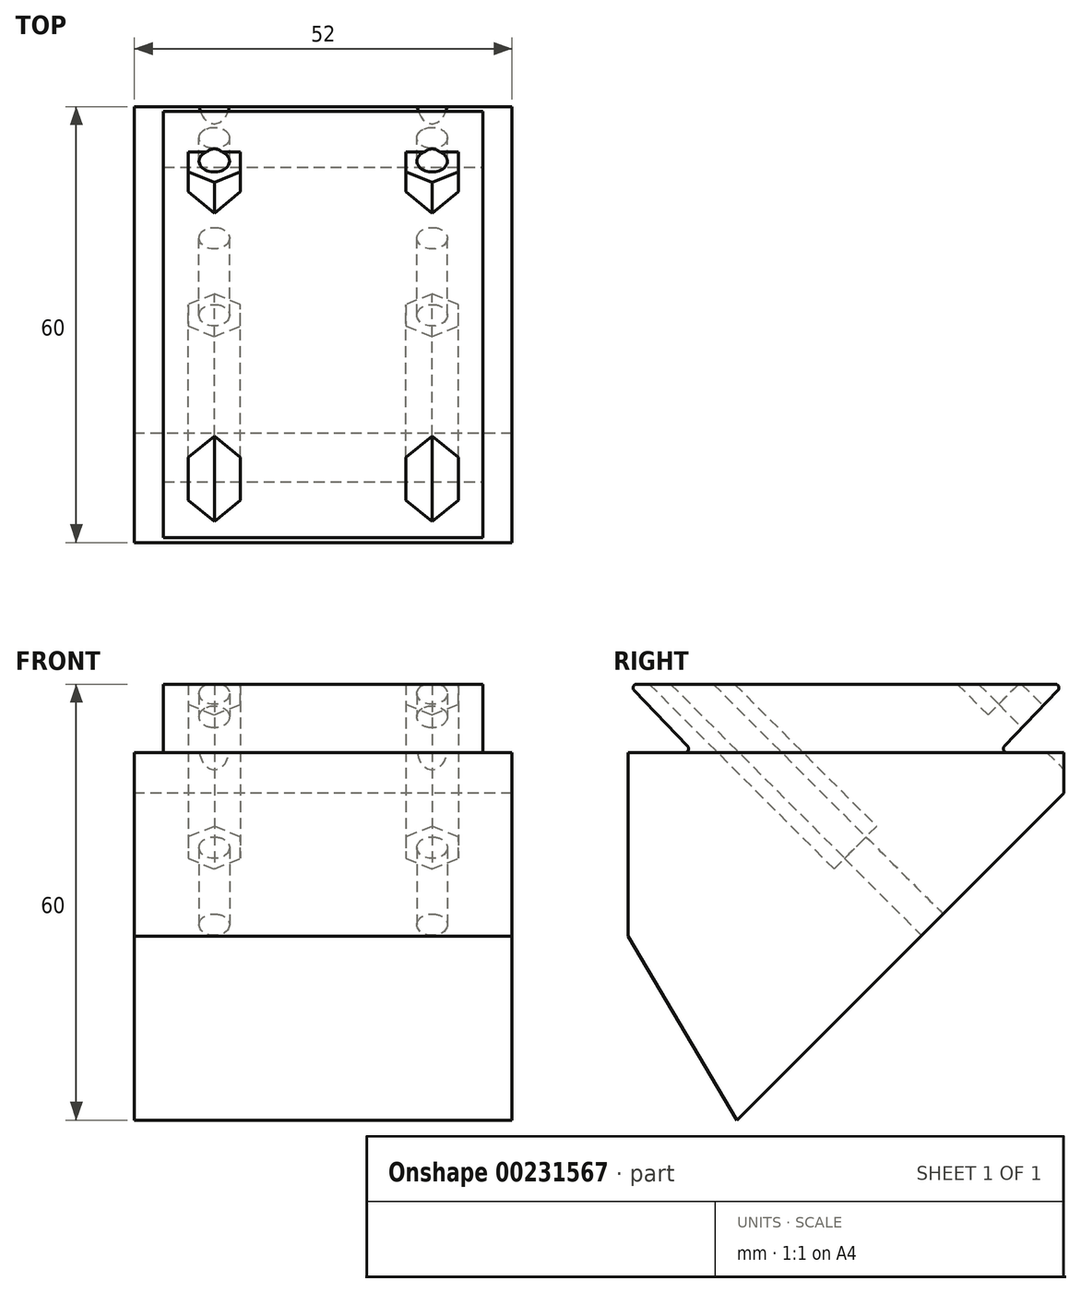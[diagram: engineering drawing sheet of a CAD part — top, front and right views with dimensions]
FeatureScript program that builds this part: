
annotation { "Feature Type Name" : "Feature", "Feature Type Description" : "" }
export const myFeature = defineFeature(function(context is Context, id is Id, definition is map)
    precondition{}
    {
        {
            var Q0;
            Q0=qCreatedBy(makeId("Top.planeOp"),FACE);
            var sketch = newSketch(context, id + "F0", { "sketchPlane" : qUnion([Q0])});
            skLineSegment(sketch, "E0.bottom", {"start": v(26, -30) * mm, "end": v(-26, -30) * mm});
            skLineSegment(sketch, "E0.top", {"start": v(26, 30) * mm, "end": v(-26, 30) * mm});
            skLineSegment(sketch, "E0.left", {"start": v(26, -30) * mm, "end": v(26, 30) * mm});
            skLineSegment(sketch, "E0.right", {"start": v(-26, -30) * mm, "end": v(-26, 30) * mm});
            skPoint(sketch, "E0.middle", {"position": v(0, 0) * mm});
            skSolve(sketch);
        }
        {
            var Q0;
            Q0=makeQuery(id+"F0.imprint","IMPRINT",FACE,{"disambiguationData":[TD([[makeQuery(id+"F0.imprint","IMPRINT",EDGE,{"derivedFrom":sQuery(id+"F0.wireOp",EDGE,"E0.bottom")}),-1.0]])]});
            extrude(context, id + "F1", {"entities" : qUnion([Q0]), "depth" : 15 * mm});
        }
        {
            var Q0;
            Q0=makeQuery(id+"F1.opExtrude","SWEPT_FACE",FACE,{"disambiguationData":[OSD([sQuery(id+"F0.wireOp",EDGE,"E0.right")])]});
            var sketch = newSketch(context, id + "F2", { "sketchPlane" : qUnion([Q0])});
            skLineSegment(sketch, "E1", {"start": v(-30, 15) * mm, "end": v(-21, 5.6) * mm});
            skLineSegment(sketch, "E2", {"start": v(-21, 5.6) * mm, "end": v(21, 5.6) * mm});
            skLineSegment(sketch, "E3", {"start": v(21, 5.6) * mm, "end": v(30, 15) * mm});
            skLineSegment(sketch, "E4", {"start": v(30, 15) * mm, "end": v(-30, 15) * mm});
            skLineSegment(sketch, "E5", {"start": v(-21, 5.6) * mm, "end": v(-30, 5.6) * mm});
            skLineSegment(sketch, "E6", {"start": v(-30, 5.6) * mm, "end": v(-30, 15) * mm});
            skLineSegment(sketch, "E7", {"start": v(21, 5.6) * mm, "end": v(30, 5.6) * mm});
            skLineSegment(sketch, "E8", {"start": v(30, 5.6) * mm, "end": v(30, 15) * mm});
            skSolve(sketch);
        }
        {
            var Q0;
            Q0=makeQuery(id+"F1.opExtrude","SWEPT_FACE",FACE,{"disambiguationData":[OSD([sQuery(id+"F0.wireOp",EDGE,"E0.top")])]});
            var sketch = newSketch(context, id + "F3", { "sketchPlane" : qUnion([Q0])});
            skLineSegment(sketch, "E9", {"start": v(-22, 15) * mm, "end": v(-22, 5.6) * mm});
            skLineSegment(sketch, "E10", {"start": v(-22, 5.6) * mm, "end": v(-26, 5.6) * mm});
            skLineSegment(sketch, "E11", {"start": v(22, 15) * mm, "end": v(22, 5.6) * mm});
            skLineSegment(sketch, "E12", {"start": v(22, 5.6) * mm, "end": v(26, 5.6) * mm});
            skSolve(sketch);
        }
        {
            var Q0;
            {var subQ0=sQuery(id+"F3.wireOp",EDGE,"E9");Q0=makeQuery(id+"F3.imprint","IMPRINT",FACE,{"disambiguationData":[TD([[makeQuery(id+"F3.imprint","IMPRINT",EDGE,{"derivedFrom":subQ0}),-1.0]])]});}
            var Q1;
            {var subQ0=sQuery(id+"F3.wireOp",EDGE,"E11");Q1=makeQuery(id+"F3.imprint","IMPRINT",FACE,{"disambiguationData":[TD([[makeQuery(id+"F3.imprint","IMPRINT",EDGE,{"derivedFrom":subQ0}),1.0]])]});}
            extrude(context, id + "F4", {"entities" : qUnion([Q0, Q1]), "operationType" : NewBodyOperationType.REMOVE, "endBound" : BoundingType.UP_TO_NEXT, "oppositeDirection" : true, "depth" : 25 * mm});
        }
        {
            var Q0;
            Q0=makeQuery(id+"F2.imprint","IMPRINT",FACE,{"disambiguationData":[TD([[makeQuery(id+"F2.imprint","IMPRINT",EDGE,{"derivedFrom":sQuery(id+"F2.wireOp",EDGE,"E1")}),-1.0]])]});
            var Q1;
            Q1=makeQuery(id+"F2.imprint","IMPRINT",FACE,{"disambiguationData":[TD([[makeQuery(id+"F2.imprint","IMPRINT",EDGE,{"derivedFrom":sQuery(id+"F2.wireOp",EDGE,"E3")}),-1.0]])]});
            extrude(context, id + "F5", {"entities" : qUnion([Q0, Q1]), "operationType" : NewBodyOperationType.REMOVE, "oppositeDirection" : true, "depth" : 56.9 * mm});
        }
        {
            var Q0;
            Q0=makeQuery(id+"F1.opExtrude","CAP_FACE",FACE,{"disambiguationData":[OSD([sQuery(id+"F0.wireOp",EDGE,"E0.bottom"),sQuery(id+"F0.wireOp",EDGE,"E0.top"),sQuery(id+"F0.wireOp",EDGE,"E0.left"),sQuery(id+"F0.wireOp",EDGE,"E0.right")])],"isStart":true});
            extrude(context, id + "F6", {"entities" : qUnion([Q0]), "operationType" : NewBodyOperationType.ADD, "depth" : 45 * mm});
        }
        {
            var Q0;
            {var subQ0=sQuery(id+"F0.wireOp",EDGE,"E0.right");Q0=makeQuery(id+"F6.boolean.opBoolean","MERGE",FACE,{"derivedFrom":[makeQuery(id+"F1.opExtrude","SWEPT_FACE",FACE,{"disambiguationData":[OSD([subQ0])]}),makeQuery(id+"F6.opExtrude","SWEPT_FACE",FACE,{"disambiguationData":[OSD([subQ0])]})]});}
            var sketch = newSketch(context, id + "F7", { "sketchPlane" : qUnion([Q0])});
            skLineSegment(sketch, "E13", {"start": v(-30, 0) * mm, "end": v(30, -60) * mm});
            skLineSegment(sketch, "E14", {"start": v(-30, 0) * mm, "end": v(-30, -45) * mm});
            skLineSegment(sketch, "E15", {"start": v(-30, -45) * mm, "end": v(15, -45) * mm});
            skSolve(sketch);
        }
        {
            var Q0;
            {var subQ0=sQuery(id+"F7.wireOp",EDGE,"E14");Q0=makeQuery(id+"F7.imprint","IMPRINT",FACE,{"disambiguationData":[TD([[makeQuery(id+"F7.imprint","IMPRINT",EDGE,{"derivedFrom":subQ0}),1.0]])]});}
            extrude(context, id + "F8", {"entities" : qUnion([Q0]), "operationType" : NewBodyOperationType.REMOVE, "oppositeDirection" : true, "depth" : 63.8 * mm});
        }
        {
            var Q0;
            Q0=makeQuery(id+"F8.boolean.opBoolean","COPY",FACE,{"derivedFrom":makeQuery(id+"F8.opExtrude","SWEPT_FACE",FACE,{"disambiguationData":[OSD([sQuery(id+"F7.wireOp",EDGE,"E13")])]})});
            var sketch = newSketch(context, id + "F9", { "sketchPlane" : qUnion([Q0])});
            skLineSegment(sketch, "E16", {"start": v(-26, -21.21) * mm, "end": v(26, 42.43) * mm, "construction": true});
            skLineSegment(sketch, "E17", {"start": v(-26, 42.43) * mm, "end": v(26, -21.21) * mm, "construction": true});
            skLineSegment(sketch, "E18.bottom", {"start": v(15, 25.6) * mm, "end": v(-15, 25.6) * mm, "construction": true});
            skLineSegment(sketch, "E18.top", {"start": v(15, -4.4) * mm, "end": v(-15, -4.4) * mm, "construction": true});
            skLineSegment(sketch, "E18.left", {"start": v(15, 25.6) * mm, "end": v(15, -4.4) * mm, "construction": true});
            skLineSegment(sketch, "E18.right", {"start": v(-15, 25.6) * mm, "end": v(-15, -4.4) * mm, "construction": true});
            skPoint(sketch, "E18.middle", {"position": v(0, 10.6) * mm});
            skCircle(sketch, "E19", {"center": v(-15, -4.4) * mm, "radius": 2.1 * mm});
            skCircle(sketch, "E20", {"center": v(-15, 25.6) * mm, "radius": 2.1 * mm});
            skCircle(sketch, "E21", {"center": v(15, 25.6) * mm, "radius": 2.1 * mm});
            skCircle(sketch, "E22", {"center": v(15, -4.4) * mm, "radius": 2.1 * mm});
            skCircle(sketch, "E23.cCircle", {"center": v(-15, -4.4) * mm, "radius": 3.6 * mm, "construction": true});
            skLineSegment(sketch, "E23.0", {"start": v(-11.4, -2.31) * mm, "end": v(-11.4, -6.47) * mm});
            skLineSegment(sketch, "E23.1", {"start": v(-11.4, -6.47) * mm, "end": v(-15, -8.55) * mm});
            skLineSegment(sketch, "E23.2", {"start": v(-15, -8.55) * mm, "end": v(-18.6, -6.47) * mm});
            skLineSegment(sketch, "E23.3", {"start": v(-18.6, -6.47) * mm, "end": v(-18.6, -2.31) * mm});
            skLineSegment(sketch, "E23.4", {"start": v(-18.6, -2.31) * mm, "end": v(-15, -0.24) * mm});
            skLineSegment(sketch, "E23.5", {"start": v(-15, -0.24) * mm, "end": v(-11.4, -2.31) * mm});
            skPoint(sketch, "E23.0.midPoint", {"position": v(-11.4, -4.4) * mm});
            skCircle(sketch, "E24.cCircle", {"center": v(-15, 25.6) * mm, "radius": 3.6 * mm, "construction": true});
            skLineSegment(sketch, "E24.0", {"start": v(-11.4, 27.69) * mm, "end": v(-11.4, 23.53) * mm});
            skLineSegment(sketch, "E24.1", {"start": v(-11.4, 23.53) * mm, "end": v(-15, 21.45) * mm});
            skLineSegment(sketch, "E24.2", {"start": v(-15, 21.45) * mm, "end": v(-18.6, 23.53) * mm});
            skLineSegment(sketch, "E24.3", {"start": v(-18.6, 23.53) * mm, "end": v(-18.6, 27.69) * mm});
            skLineSegment(sketch, "E24.4", {"start": v(-18.6, 27.69) * mm, "end": v(-15, 29.76) * mm});
            skLineSegment(sketch, "E24.5", {"start": v(-15, 29.76) * mm, "end": v(-11.4, 27.69) * mm});
            skPoint(sketch, "E24.0.midPoint", {"position": v(-11.4, 25.6) * mm});
            skCircle(sketch, "E25.cCircle", {"center": v(15, 25.6) * mm, "radius": 3.6 * mm, "construction": true});
            skLineSegment(sketch, "E25.0", {"start": v(11.4, 23.53) * mm, "end": v(11.4, 27.69) * mm});
            skLineSegment(sketch, "E25.1", {"start": v(11.4, 27.69) * mm, "end": v(15, 29.76) * mm});
            skLineSegment(sketch, "E25.2", {"start": v(15, 29.76) * mm, "end": v(18.6, 27.69) * mm});
            skLineSegment(sketch, "E25.3", {"start": v(18.6, 27.69) * mm, "end": v(18.6, 23.53) * mm});
            skLineSegment(sketch, "E25.4", {"start": v(18.6, 23.53) * mm, "end": v(15, 21.45) * mm});
            skLineSegment(sketch, "E25.5", {"start": v(15, 21.45) * mm, "end": v(11.4, 23.53) * mm});
            skPoint(sketch, "E25.0.midPoint", {"position": v(11.4, 25.6) * mm});
            skCircle(sketch, "E26.cCircle", {"center": v(15, -4.4) * mm, "radius": 3.6 * mm, "construction": true});
            skLineSegment(sketch, "E26.0", {"start": v(11.4, -6.47) * mm, "end": v(11.4, -2.31) * mm});
            skLineSegment(sketch, "E26.1", {"start": v(11.4, -2.31) * mm, "end": v(15, -0.24) * mm});
            skLineSegment(sketch, "E26.2", {"start": v(15, -0.24) * mm, "end": v(18.6, -2.31) * mm});
            skLineSegment(sketch, "E26.3", {"start": v(18.6, -2.31) * mm, "end": v(18.6, -6.47) * mm});
            skLineSegment(sketch, "E26.4", {"start": v(18.6, -6.47) * mm, "end": v(15, -8.55) * mm});
            skLineSegment(sketch, "E26.5", {"start": v(15, -8.55) * mm, "end": v(11.4, -6.47) * mm});
            skPoint(sketch, "E26.0.midPoint", {"position": v(11.4, -4.4) * mm});
            skSolve(sketch);
        }
        {
            var Q0;
            Q0=makeQuery(id+"F9.imprint","IMPRINT",FACE,{"disambiguationData":[TD([[makeQuery(id+"F9.imprint","IMPRINT",EDGE,{"derivedFrom":sQuery(id+"F9.wireOp",EDGE,"E19")}),1.0]])]});
            var Q1;
            Q1=makeQuery(id+"F9.imprint","IMPRINT",FACE,{"disambiguationData":[TD([[makeQuery(id+"F9.imprint","IMPRINT",EDGE,{"derivedFrom":sQuery(id+"F9.wireOp",EDGE,"E20")}),1.0]])]});
            var Q2;
            Q2=makeQuery(id+"F9.imprint","IMPRINT",FACE,{"disambiguationData":[TD([[makeQuery(id+"F9.imprint","IMPRINT",EDGE,{"derivedFrom":sQuery(id+"F9.wireOp",EDGE,"E22")}),1.0]])]});
            var Q3;
            Q3=makeQuery(id+"F9.imprint","IMPRINT",FACE,{"disambiguationData":[TD([[makeQuery(id+"F9.imprint","IMPRINT",EDGE,{"derivedFrom":sQuery(id+"F9.wireOp",EDGE,"E21")}),1.0]])]});
            extrude(context, id + "F10", {"entities" : qUnion([Q0, Q1, Q2, Q3]), "operationType" : NewBodyOperationType.REMOVE, "oppositeDirection" : true, "depth" : 101.4 * mm});
        }
        {
            var Q0;
            Q0=makeQuery(id+"F9.imprint","IMPRINT",FACE,{"disambiguationData":[TD([[makeQuery(id+"F9.imprint","IMPRINT",EDGE,{"derivedFrom":sQuery(id+"F9.wireOp",EDGE,"E19")}),-1.0]])]});
            var Q1;
            Q1=makeQuery(id+"F9.imprint","IMPRINT",FACE,{"disambiguationData":[TD([[makeQuery(id+"F9.imprint","IMPRINT",EDGE,{"derivedFrom":sQuery(id+"F9.wireOp",EDGE,"E20")}),-1.0]])]});
            var Q2;
            Q2=makeQuery(id+"F9.imprint","IMPRINT",FACE,{"disambiguationData":[TD([[makeQuery(id+"F9.imprint","IMPRINT",EDGE,{"derivedFrom":sQuery(id+"F9.wireOp",EDGE,"E21")}),-1.0]])]});
            var Q3;
            Q3=makeQuery(id+"F9.imprint","IMPRINT",FACE,{"disambiguationData":[TD([[makeQuery(id+"F9.imprint","IMPRINT",EDGE,{"derivedFrom":sQuery(id+"F9.wireOp",EDGE,"E22")}),-1.0]])]});
            extrude(context, id + "F11", {"entities" : qUnion([Q0, Q1, Q2, Q3]), "operationType" : NewBodyOperationType.REMOVE, "oppositeDirection" : true, "depth" : 64.6 * mm, "hasSecondDirection" : true, "secondDirectionOppositeDirection" : true, "secondDirectionDepth" : 15 * mm});
        }
        {
            var Q0;
            {var subQ0=sQuery(id+"F0.wireOp",EDGE,"E0.right");Q0=makeQuery(id+"F6.boolean.opBoolean","MERGE",FACE,{"derivedFrom":[makeQuery(id+"F1.opExtrude","SWEPT_FACE",FACE,{"disambiguationData":[OSD([subQ0])]}),makeQuery(id+"F6.opExtrude","SWEPT_FACE",FACE,{"disambiguationData":[OSD([subQ0])]})]});}
            var sketch = newSketch(context, id + "F12", { "sketchPlane" : qUnion([Q0])});
            skLineSegment(sketch, "E27", {"start": v(15, -45) * mm, "end": v(30, -19.7) * mm});
            skLineSegment(sketch, "E28", {"start": v(30, -19.7) * mm, "end": v(30, -45) * mm});
            skLineSegment(sketch, "E29", {"start": v(30, -45) * mm, "end": v(15, -45) * mm});
            skSolve(sketch);
        }
        {
            var Q0;
            Q0 = qSketchRegion(id + "F12", true);
            extrude(context, id + "F13", {"entities" : qUnion([Q0]), "operationType" : NewBodyOperationType.REMOVE, "oppositeDirection" : true, "depth" : 115.6 * mm});
        }
        {
            var Q0;
            Q0=makeQuery(id+"F5.boolean.opBoolean","MERGE",EDGE,{"derivedFrom":[makeQuery(id+"F4.boolean.opBoolean","COPY",EDGE,{"derivedFrom":makeQuery(id+"F4.opExtrude","CAP_EDGE",EDGE,{"disambiguationData":[OSD([sQuery(id+"F3.wireOp",EDGE,"E10")])],"isStart":false})}),makeQuery(id+"F4.boolean.opBoolean","COPY",EDGE,{"derivedFrom":makeQuery(id+"F4.opExtrude","CAP_EDGE",EDGE,{"disambiguationData":[OSD([sQuery(id+"F3.wireOp",EDGE,"E12")])],"isStart":false})})],"fromTools":[makeQuery(id+"F5.opExtrude","SWEPT_EDGE",EDGE,{"disambiguationData":[OSD([sQuery(id+"F0.wireOp",EDGE,"E0.bottom"),sQuery(id+"F0.wireOp",EDGE,"E0.right"),sQuery(id+"F2.wireOp",EDGE,"E7"),sQuery(id+"F2.wireOp",EDGE,"E8")])]})]});
            var Q1;
            Q1=makeQuery(id+"F13.boolean.opBoolean","COPY",EDGE,{"derivedFrom":makeQuery(id+"F13.opExtrude","SWEPT_EDGE",EDGE,{"disambiguationData":[OSD([sQuery(id+"F0.wireOp",EDGE,"E0.bottom"),sQuery(id+"F0.wireOp",EDGE,"E0.right"),sQuery(id+"F12.wireOp",EDGE,"E27"),sQuery(id+"F12.wireOp",EDGE,"E28")])]})});
            var Q2;
            Q2=makeQuery(id+"F5.boolean.opBoolean","MERGE",EDGE,{"derivedFrom":[makeQuery(id+"F4.boolean.opBoolean","COPY",EDGE,{"derivedFrom":makeQuery(id+"F4.opExtrude","CAP_EDGE",EDGE,{"disambiguationData":[OSD([sQuery(id+"F3.wireOp",EDGE,"E10")])],"isStart":true})}),makeQuery(id+"F4.boolean.opBoolean","COPY",EDGE,{"derivedFrom":makeQuery(id+"F4.opExtrude","CAP_EDGE",EDGE,{"disambiguationData":[OSD([sQuery(id+"F3.wireOp",EDGE,"E12")])],"isStart":true})})],"fromTools":[makeQuery(id+"F5.opExtrude","SWEPT_EDGE",EDGE,{"disambiguationData":[OSD([sQuery(id+"F0.wireOp",EDGE,"E0.top"),sQuery(id+"F0.wireOp",EDGE,"E0.right"),sQuery(id+"F2.wireOp",EDGE,"E5"),sQuery(id+"F2.wireOp",EDGE,"E6")])]})]});
            var Q3;
            Q3=makeQuery(id+"F5.boolean.opBoolean","MERGE",EDGE,{"derivedFrom":[makeQuery(id+"F1.opExtrude","CAP_EDGE",EDGE,{"disambiguationData":[OSD([sQuery(id+"F0.wireOp",EDGE,"E0.bottom")])],"isStart":false}),makeQuery(id+"F5.opExtrude","SWEPT_EDGE",EDGE,{"disambiguationData":[OSD([sQuery(id+"F2.wireOp",EDGE,"E3"),sQuery(id+"F2.wireOp",EDGE,"E4"),sQuery(id+"F2.wireOp",EDGE,"E8")])]})]});
            var Q4;
            Q4=makeQuery(id+"F5.boolean.opBoolean","MERGE",EDGE,{"derivedFrom":[makeQuery(id+"F1.opExtrude","CAP_EDGE",EDGE,{"disambiguationData":[OSD([sQuery(id+"F0.wireOp",EDGE,"E0.top")])],"isStart":false}),makeQuery(id+"F5.opExtrude","SWEPT_EDGE",EDGE,{"disambiguationData":[OSD([sQuery(id+"F2.wireOp",EDGE,"E1"),sQuery(id+"F2.wireOp",EDGE,"E4"),sQuery(id+"F2.wireOp",EDGE,"E6")])]})]});
            var Q5;
            Q5=makeQuery(id+"F5.boolean.opBoolean","COPY",EDGE,{"derivedFrom":makeQuery(id+"F5.opExtrude","SWEPT_EDGE",EDGE,{"disambiguationData":[OSD([sQuery(id+"F2.wireOp",EDGE,"E2"),sQuery(id+"F2.wireOp",EDGE,"E3"),sQuery(id+"F2.wireOp",EDGE,"E7")])]})});
            var Q6;
            Q6=makeQuery(id+"F5.boolean.opBoolean","COPY",EDGE,{"derivedFrom":makeQuery(id+"F5.opExtrude","SWEPT_EDGE",EDGE,{"disambiguationData":[OSD([sQuery(id+"F2.wireOp",EDGE,"E1"),sQuery(id+"F2.wireOp",EDGE,"E2"),sQuery(id+"F2.wireOp",EDGE,"E5")])]})});
            var Q7;
            Q7=makeQuery(id+"F8.boolean.opBoolean","COPY",EDGE,{"derivedFrom":makeQuery(id+"F8.opExtrude","SWEPT_EDGE",EDGE,{"disambiguationData":[OSD([sQuery(id+"F0.wireOp",EDGE,"E0.top"),sQuery(id+"F0.wireOp",EDGE,"E0.right"),sQuery(id+"F7.wireOp",EDGE,"E13"),sQuery(id+"F7.wireOp",EDGE,"E14")])]})});
            var Q8;
            {var subQ0=sQuery(id+"F7.wireOp",EDGE,"E13");Q8=makeQuery(id+"F13.boolean.opBoolean","MERGE",EDGE,{"derivedFrom":[makeQuery(id+"F8.boolean.opBoolean","COPY",EDGE,{"derivedFrom":makeQuery(id+"F8.opExtrude","SWEPT_EDGE",EDGE,{"disambiguationData":[OSD([sQuery(id+"F0.wireOp",EDGE,"E0.right"),subQ0,sQuery(id+"F7.wireOp",EDGE,"E15")])]})}),makeQuery(id+"F13.opExtrude","SWEPT_EDGE",EDGE,{"disambiguationData":[OSD([subQ0,sQuery(id+"F12.wireOp",EDGE,"E27"),sQuery(id+"F12.wireOp",EDGE,"E29")])]})]});}
            fillet(context, id + "F14", {"entities" : qUnion([Q0, Q1, Q2, Q3, Q4, Q5, Q6, Q7, Q8]), "radius" : 0.5 * mm, "tangentPropagation" : true, "allowEdgeOverflow" : false});
        }
    });
